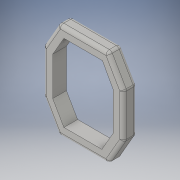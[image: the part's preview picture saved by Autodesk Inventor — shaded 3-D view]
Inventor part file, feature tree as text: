
AUTODESK INVENTOR PART (.ipt)
format: ipt  version: 2016 (Build 200138000, 138)  size: 158,208 bytes
history: native  units: in
note: dims shown in document units (in); Inventor stores cm internally (conversion verified against a paired STEP export)
features: extrude x1, fillet x1, sketch x1
ambient origin geometry x8: Origin, YZ Plane, XZ Plane, XY Plane, X Axis, Y Axis, Z Axis, Center Point
bodies: Solid1 (feature_tree)
feature tree (3):
  extrude  "Extrusion1"  Depth=3.5in
  fillet  "Fillet1"  Radius=3.5in
  sketch  "Sketch1"  dims[d0=3.5in d1=3.5in d2=3.5in d3=3.5in d4=3.5in d5=5.0in d6=0.0in d7=1.25in d8=3.5in]
